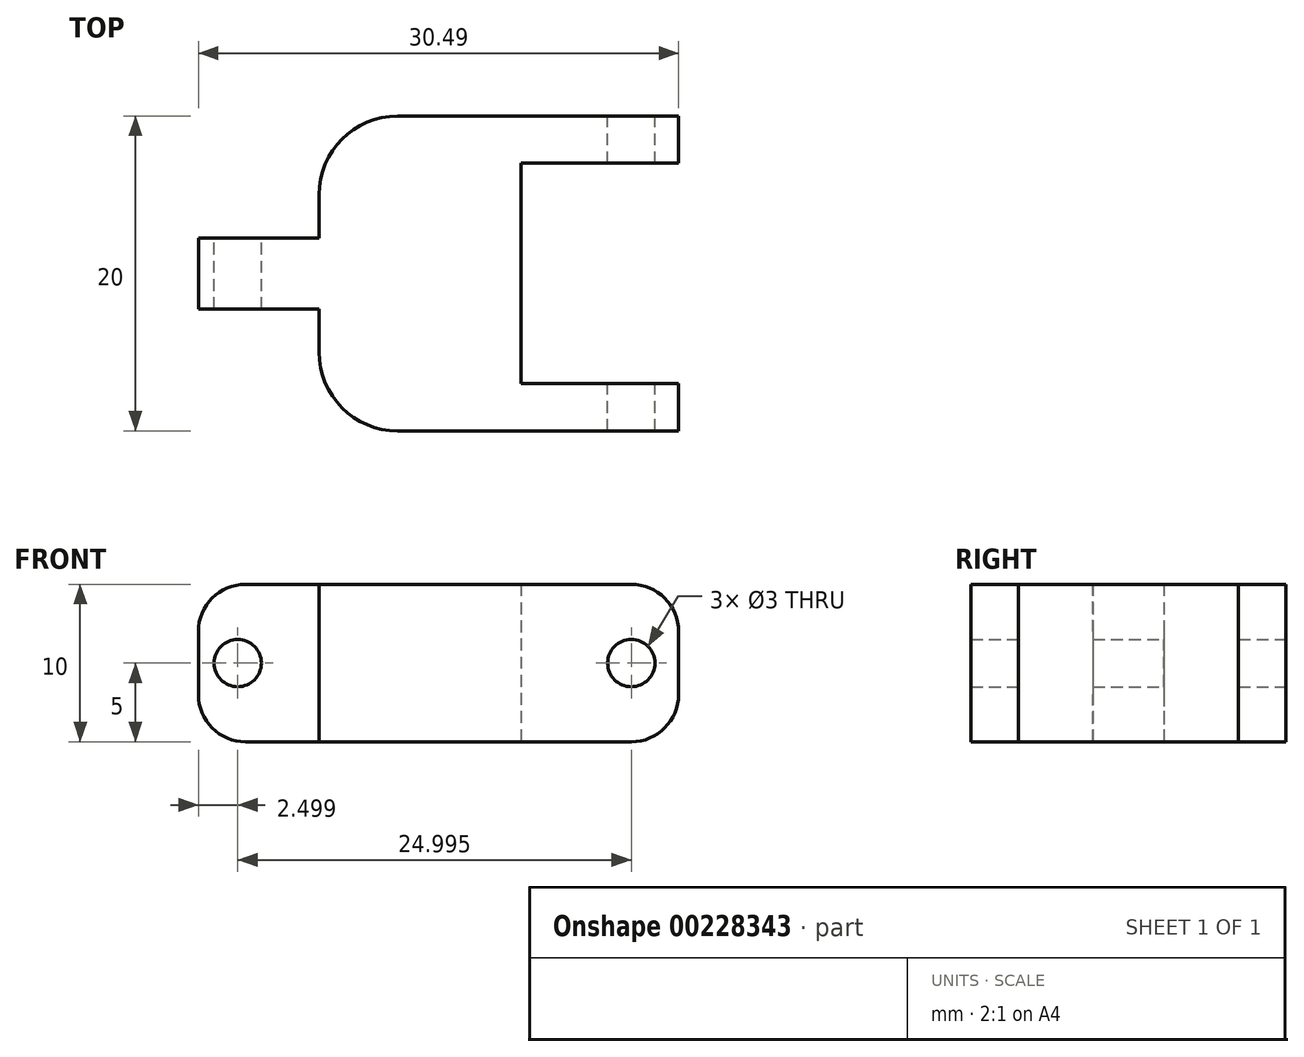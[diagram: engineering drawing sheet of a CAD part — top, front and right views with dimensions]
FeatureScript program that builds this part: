
annotation { "Feature Type Name" : "Feature", "Feature Type Description" : "" }
export const myFeature = defineFeature(function(context is Context, id is Id, definition is map)
    precondition{}
    {
        {
            var Q0;
            Q0=qCreatedBy(makeId("Top.planeOp"),FACE);
            var sketch = newSketch(context, id + "F0", { "sketchPlane" : qUnion([Q0])});
            skLineSegment(sketch, "E0.bottom", {"start": v(-44.38, 48.64) * mm, "end": v(-26.55, 48.64) * mm});
            skLineSegment(sketch, "E0.top", {"start": v(-44.38, 28.64) * mm, "end": v(-26.55, 28.64) * mm});
            skLineSegment(sketch, "E0.left", {"start": v(-57.04, 40.89) * mm, "end": v(-57.04, 36.39) * mm});
            skLineSegment(sketch, "E0.right", {"start": v(-26.55, 48.64) * mm, "end": v(-26.55, 45.64) * mm});
            skLineSegment(sketch, "E1", {"start": v(-26.55, 45.64) * mm, "end": v(-36.55, 45.64) * mm});
            skLineSegment(sketch, "E2", {"start": v(-36.55, 45.64) * mm, "end": v(-36.55, 31.64) * mm});
            skLineSegment(sketch, "E3", {"start": v(-36.55, 31.64) * mm, "end": v(-26.55, 31.64) * mm});
            skLineSegment(sketch, "E4.trimOffspring", {"start": v(-26.55, 31.64) * mm, "end": v(-26.55, 28.64) * mm});
            skLineSegment(sketch, "E5", {"start": v(-49.38, 43.64) * mm, "end": v(-49.38, 40.89) * mm});
            skLineSegment(sketch, "E6", {"start": v(-49.38, 40.89) * mm, "end": v(-57.04, 40.89) * mm});
            skLineSegment(sketch, "E7", {"start": v(-57.04, 36.39) * mm, "end": v(-49.38, 36.39) * mm});
            skLineSegment(sketch, "E8", {"start": v(-49.38, 36.39) * mm, "end": v(-49.38, 33.64) * mm});
            skPoint(sketch, "E9.visualSharp", {"position": v(-49.38, 48.64) * mm});
            skArc(sketch, "E9.filletArc", {"start": v(-44.38, 48.64) * mm, "mid": v(-47.92, 47.17) * mm, "end": v(-49.38, 43.64) * mm});
            skPoint(sketch, "E10.visualSharp", {"position": v(-49.38, 28.64) * mm});
            skArc(sketch, "E10.filletArc", {"start": v(-49.38, 33.64) * mm, "mid": v(-47.92, 30.1) * mm, "end": v(-44.38, 28.64) * mm});
            skSolve(sketch);
        }
        {
            var Q0;
            Q0=makeQuery(id+"F0.imprint","IMPRINT",FACE,{"disambiguationData":[TD([[makeQuery(id+"F0.imprint","IMPRINT",EDGE,{"derivedFrom":sQuery(id+"F0.wireOp",EDGE,"E0.bottom")}),-1.0]])]});
            extrude(context, id + "F1", {"entities" : qUnion([Q0]), "depth" : 10 * mm});
        }
        {
            var Q0;
            Q0=makeQuery(id+"F1.opExtrude","SWEPT_FACE",FACE,{"disambiguationData":[OSD([sQuery(id+"F0.wireOp",EDGE,"E0.bottom")])]});
            var sketch = newSketch(context, id + "F2", { "sketchPlane" : qUnion([Q0])});
            skCircle(sketch, "E11", {"center": v(29.55, 5) * mm, "radius": 1.5 * mm});
            skPoint(sketch, "E11.centerSnap0", {"position": v(26.55, 5) * mm});
            skCircle(sketch, "E12", {"center": v(54.54, 5) * mm, "radius": 1.5 * mm});
            skSolve(sketch);
        }
        {
            var Q0;
            Q0=makeQuery(id+"F2.imprint","IMPRINT",FACE,{"disambiguationData":[TD([[makeQuery(id+"F2.imprint","IMPRINT",EDGE,{"derivedFrom":sQuery(id+"F2.wireOp",EDGE,"E12")}),1.0]])]});
            var Q1;
            Q1=makeQuery(id+"F2.imprint","IMPRINT",FACE,{"disambiguationData":[TD([[makeQuery(id+"F2.imprint","IMPRINT",EDGE,{"derivedFrom":sQuery(id+"F2.wireOp",EDGE,"E11")}),1.0]])]});
            extrude(context, id + "F3", {"entities" : qUnion([Q0, Q1]), "operationType" : NewBodyOperationType.REMOVE, "oppositeDirection" : true, "depth" : 25 * mm});
        }
        {
            var Q0;
            Q0=makeQuery(id+"F1.opExtrude","CAP_EDGE",EDGE,{"disambiguationData":[OSD([sQuery(id+"F0.wireOp",EDGE,"E0.left")])],"isStart":false});
            var Q1;
            Q1=makeQuery(id+"F1.opExtrude","CAP_EDGE",EDGE,{"disambiguationData":[OSD([sQuery(id+"F0.wireOp",EDGE,"E0.left")])],"isStart":true});
            var Q2;
            Q2=makeQuery(id+"F1.opExtrude","CAP_EDGE",EDGE,{"disambiguationData":[OSD([sQuery(id+"F0.wireOp",EDGE,"E0.right")])],"isStart":false});
            var Q3;
            Q3=makeQuery(id+"F1.opExtrude","CAP_EDGE",EDGE,{"disambiguationData":[OSD([sQuery(id+"F0.wireOp",EDGE,"E4.trimOffspring")])],"isStart":false});
            var Q4;
            Q4=makeQuery(id+"F1.opExtrude","CAP_EDGE",EDGE,{"disambiguationData":[OSD([sQuery(id+"F0.wireOp",EDGE,"E0.right")])],"isStart":true});
            var Q5;
            Q5=makeQuery(id+"F1.opExtrude","CAP_EDGE",EDGE,{"disambiguationData":[OSD([sQuery(id+"F0.wireOp",EDGE,"E4.trimOffspring")])],"isStart":true});
            fillet(context, id + "F4", {"entities" : qUnion([Q0, Q1, Q2, Q3, Q4, Q5]), "radius" : 3 * mm, "tangentPropagation" : true, "allowEdgeOverflow" : false});
        }
    });
